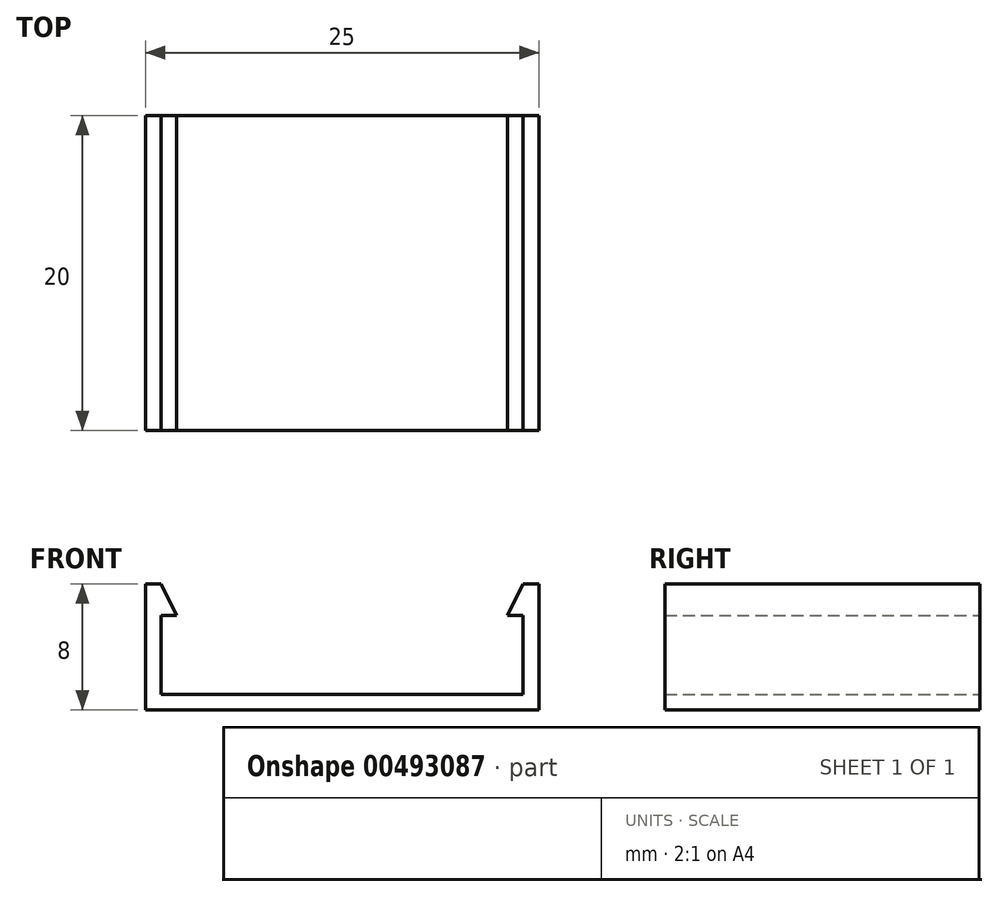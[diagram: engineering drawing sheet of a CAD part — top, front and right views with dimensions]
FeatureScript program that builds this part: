
annotation { "Feature Type Name" : "Feature", "Feature Type Description" : "" }
export const myFeature = defineFeature(function(context is Context, id is Id, definition is map)
    precondition{}
    {
        {
            var Q0;
            Q0=qCreatedBy(makeId("Front.planeOp"),FACE);
            var sketch = newSketch(context, id + "F0", { "sketchPlane" : qUnion([Q0])});
            skLineSegment(sketch, "E0", {"start": v(-12.45, 0) * mm, "end": v(12.55, 0) * mm});
            skLineSegment(sketch, "E1", {"start": v(-12.45, 0) * mm, "end": v(-12.45, 8) * mm});
            skLineSegment(sketch, "E2", {"start": v(12.55, 0) * mm, "end": v(12.55, 8) * mm});
            skLineSegment(sketch, "E3", {"start": v(12.55, 8) * mm, "end": v(11.55, 8) * mm});
            skLineSegment(sketch, "E4", {"start": v(11.55, 8) * mm, "end": v(10.55, 6) * mm});
            skLineSegment(sketch, "E5", {"start": v(10.55, 6) * mm, "end": v(11.55, 6) * mm});
            skLineSegment(sketch, "E6", {"start": v(11.55, 6) * mm, "end": v(11.55, 1) * mm});
            skLineSegment(sketch, "E7", {"start": v(11.55, 1) * mm, "end": v(-11.45, 1) * mm});
            skLineSegment(sketch, "E8", {"start": v(-11.45, 1) * mm, "end": v(-11.45, 6) * mm});
            skLineSegment(sketch, "E9", {"start": v(-11.45, 6) * mm, "end": v(-10.45, 6) * mm});
            skLineSegment(sketch, "E10", {"start": v(-10.45, 6) * mm, "end": v(-11.45, 8) * mm});
            skLineSegment(sketch, "E11", {"start": v(-11.45, 8) * mm, "end": v(-12.45, 8) * mm});
            skSolve(sketch);
        }
        {
            var Q0;
            Q0=makeQuery(id+"F0.imprint","IMPRINT",FACE,{"disambiguationData":[TD([[makeQuery(id+"F0.imprint","IMPRINT",EDGE,{"derivedFrom":sQuery(id+"F0.wireOp",EDGE,"E0")}),1.0]])]});
            extrude(context, id + "F1", {"entities" : qUnion([Q0]), "depth" : 20 * mm});
        }
    });
